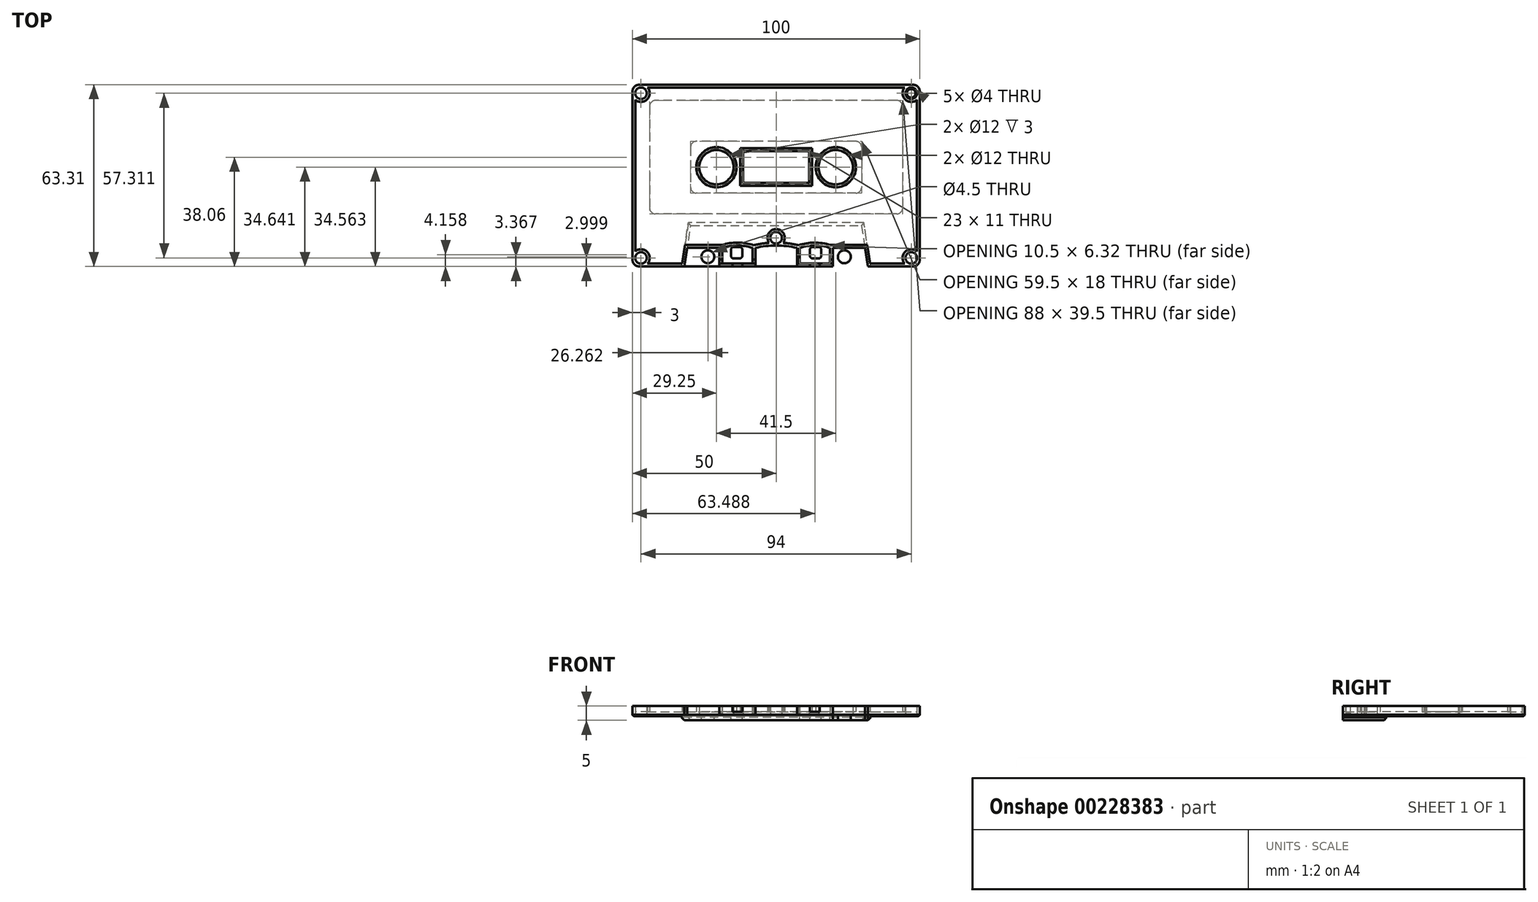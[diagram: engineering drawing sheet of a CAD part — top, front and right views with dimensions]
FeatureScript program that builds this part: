
annotation { "Feature Type Name" : "Feature", "Feature Type Description" : "" }
export const myFeature = defineFeature(function(context is Context, id is Id, definition is map)
    precondition{}
    {
        {
            var Q0;
            Q0=qCreatedBy(makeId("Top.planeOp"),FACE);
            var sketch = newSketch(context, id + "F0", { "sketchPlane" : qUnion([Q0])});
            skLineSegment(sketch, "E0.bottom", {"start": v(-47.5, 0) * mm, "end": v(47.5, 0) * mm});
            skLineSegment(sketch, "E0.top", {"start": v(-47.5, -63.31) * mm, "end": v(47.5, -63.31) * mm});
            skLineSegment(sketch, "E0.left", {"start": v(-50, -2.5) * mm, "end": v(-50, -60.81) * mm});
            skLineSegment(sketch, "E0.right", {"start": v(50, -2.5) * mm, "end": v(50, -60.81) * mm});
            skPoint(sketch, "E0.middle", {"position": v(0, -31.66) * mm});
            skLineSegment(sketch, "E1", {"start": v(0, -65.66) * mm, "end": v(0, 8.32) * mm, "construction": true});
            skLineSegment(sketch, "E2.bottom", {"start": v(42, -5.5) * mm, "end": v(-42, -5.5) * mm});
            skLineSegment(sketch, "E2.top", {"start": v(42, -45) * mm, "end": v(-42, -45) * mm});
            skLineSegment(sketch, "E2.left", {"start": v(44, -7.5) * mm, "end": v(44, -43) * mm});
            skLineSegment(sketch, "E2.right", {"start": v(-44, -7.5) * mm, "end": v(-44, -43) * mm});
            skPoint(sketch, "E2.middle", {"position": v(0, -25.25) * mm});
            skPoint(sketch, "E3.visualSharp", {"position": v(-44, -5.5) * mm});
            skArc(sketch, "E3.filletArc", {"start": v(-42, -5.5) * mm, "mid": v(-43.41, -6.09) * mm, "end": v(-44, -7.5) * mm});
            skPoint(sketch, "E4.visualSharp", {"position": v(-44, -45) * mm});
            skArc(sketch, "E4.filletArc", {"start": v(-44, -43) * mm, "mid": v(-43.41, -44.41) * mm, "end": v(-42, -45) * mm});
            skPoint(sketch, "E5.visualSharp", {"position": v(44, -5.5) * mm});
            skArc(sketch, "E5.filletArc", {"start": v(44, -7.5) * mm, "mid": v(43.41, -6.09) * mm, "end": v(42, -5.5) * mm});
            skPoint(sketch, "E6.visualSharp", {"position": v(44, -45) * mm});
            skArc(sketch, "E6.filletArc", {"start": v(42, -45) * mm, "mid": v(43.41, -44.41) * mm, "end": v(44, -43) * mm});
            skLineSegment(sketch, "E7.bottom", {"start": v(27.75, -19.75) * mm, "end": v(-27.75, -19.75) * mm});
            skLineSegment(sketch, "E7.top", {"start": v(27.75, -37.75) * mm, "end": v(-27.75, -37.75) * mm});
            skLineSegment(sketch, "E7.left", {"start": v(29.75, -21.75) * mm, "end": v(29.75, -35.75) * mm});
            skLineSegment(sketch, "E7.right", {"start": v(-29.75, -21.75) * mm, "end": v(-29.75, -35.75) * mm});
            skPoint(sketch, "E7.middle", {"position": v(0, -28.75) * mm});
            skPoint(sketch, "E8.visualSharp", {"position": v(-29.75, -19.75) * mm});
            skArc(sketch, "E8.filletArc", {"start": v(-27.75, -19.75) * mm, "mid": v(-29.16, -20.33) * mm, "end": v(-29.75, -21.75) * mm});
            skPoint(sketch, "E9.visualSharp", {"position": v(-29.75, -37.75) * mm});
            skArc(sketch, "E9.filletArc", {"start": v(-29.75, -35.75) * mm, "mid": v(-29.16, -37.16) * mm, "end": v(-27.75, -37.75) * mm});
            skPoint(sketch, "E10.visualSharp", {"position": v(29.75, -19.75) * mm});
            skArc(sketch, "E10.filletArc", {"start": v(29.75, -21.75) * mm, "mid": v(29.16, -20.33) * mm, "end": v(27.75, -19.75) * mm});
            skPoint(sketch, "E11.visualSharp", {"position": v(29.75, -37.75) * mm});
            skArc(sketch, "E11.filletArc", {"start": v(27.75, -37.75) * mm, "mid": v(29.16, -37.16) * mm, "end": v(29.75, -35.75) * mm});
            skPoint(sketch, "E12.visualSharp", {"position": v(-50, 0) * mm});
            skArc(sketch, "E12.filletArc", {"start": v(-47.5, 0) * mm, "mid": v(-49.27, -0.73) * mm, "end": v(-50, -2.5) * mm});
            skPoint(sketch, "E13.visualSharp", {"position": v(-50, -63.31) * mm});
            skArc(sketch, "E13.filletArc", {"start": v(-50, -60.81) * mm, "mid": v(-49.27, -62.58) * mm, "end": v(-47.5, -63.31) * mm});
            skPoint(sketch, "E14.visualSharp", {"position": v(50, -63.31) * mm});
            skArc(sketch, "E14.filletArc", {"start": v(47.5, -63.31) * mm, "mid": v(49.27, -62.58) * mm, "end": v(50, -60.81) * mm});
            skPoint(sketch, "E15.visualSharp", {"position": v(50, 0) * mm});
            skArc(sketch, "E15.filletArc", {"start": v(50, -2.5) * mm, "mid": v(49.27, -0.73) * mm, "end": v(47.5, 0) * mm});
            skCircle(sketch, "E16.0", {"center": v(-20.75, -28.75) * mm, "radius": 6 * mm});
            skLineSegment(sketch, "E17.bottom", {"start": v(11.5, -23.17) * mm, "end": v(-11.5, -23.17) * mm});
            skLineSegment(sketch, "E17.top", {"start": v(11.5, -34.17) * mm, "end": v(-11.5, -34.17) * mm});
            skLineSegment(sketch, "E17.left", {"start": v(11.5, -23.17) * mm, "end": v(11.5, -34.17) * mm});
            skLineSegment(sketch, "E17.right", {"start": v(-11.5, -23.17) * mm, "end": v(-11.5, -34.17) * mm});
            skPoint(sketch, "E17.middle", {"position": v(0, -28.67) * mm});
            skLineSegment(sketch, "E18.bottom", {"start": v(-14.74, -56.51) * mm, "end": v(-12.74, -56.51) * mm});
            skLineSegment(sketch, "E18.top", {"start": v(-14.74, -60.51) * mm, "end": v(-12.74, -60.51) * mm});
            skLineSegment(sketch, "E18.left", {"start": v(-15.74, -57.51) * mm, "end": v(-15.74, -59.51) * mm});
            skLineSegment(sketch, "E18.right", {"start": v(-11.74, -57.51) * mm, "end": v(-11.74, -59.51) * mm});
            skPoint(sketch, "E19.visualSharp", {"position": v(-15.74, -56.51) * mm});
            skArc(sketch, "E19.filletArc", {"start": v(-14.74, -56.51) * mm, "mid": v(-15.44, -56.8) * mm, "end": v(-15.74, -57.51) * mm});
            skPoint(sketch, "E20.visualSharp", {"position": v(-11.74, -56.51) * mm});
            skArc(sketch, "E20.filletArc", {"start": v(-11.74, -57.51) * mm, "mid": v(-12.03, -56.8) * mm, "end": v(-12.74, -56.51) * mm});
            skPoint(sketch, "E21.visualSharp", {"position": v(-11.74, -60.51) * mm});
            skArc(sketch, "E21.filletArc", {"start": v(-12.74, -60.51) * mm, "mid": v(-12.03, -60.22) * mm, "end": v(-11.74, -59.51) * mm});
            skPoint(sketch, "E22.visualSharp", {"position": v(-15.74, -60.51) * mm});
            skArc(sketch, "E22.filletArc", {"start": v(-15.74, -59.51) * mm, "mid": v(-15.44, -60.22) * mm, "end": v(-14.74, -60.51) * mm});
            skCircle(sketch, "E23", {"center": v(-23.74, -59.94) * mm, "radius": 2.25 * mm});
            skArc(sketch, "E24.MirrorCS", {"start": v(11.74, -57.51) * mm, "mid": v(12.03, -56.8) * mm, "end": v(12.74, -56.51) * mm});
            skArc(sketch, "E25.MirrorCS", {"start": v(12.74, -60.51) * mm, "mid": v(12.03, -60.22) * mm, "end": v(11.74, -59.51) * mm});
            skArc(sketch, "E26.MirrorCS", {"start": v(14.74, -56.51) * mm, "mid": v(15.44, -56.8) * mm, "end": v(15.74, -57.51) * mm});
            skLineSegment(sketch, "E27.MirrorCS", {"start": v(14.74, -56.51) * mm, "end": v(12.74, -56.51) * mm});
            skArc(sketch, "E28.MirrorCS", {"start": v(15.74, -59.51) * mm, "mid": v(15.44, -60.22) * mm, "end": v(14.74, -60.51) * mm});
            skLineSegment(sketch, "E29.MirrorCS", {"start": v(14.74, -60.51) * mm, "end": v(12.74, -60.51) * mm});
            skLineSegment(sketch, "E30.MirrorCS", {"start": v(15.74, -57.51) * mm, "end": v(15.74, -59.51) * mm});
            skPoint(sketch, "E31.MirrorP", {"position": v(15.74, -56.51) * mm});
            skCircle(sketch, "E32.MirrorC", {"center": v(23.74, -59.94) * mm, "radius": 2.25 * mm});
            skPoint(sketch, "E33.MirrorP", {"position": v(11.74, -56.51) * mm});
            skPoint(sketch, "E34.MirrorP", {"position": v(15.74, -60.51) * mm});
            skLineSegment(sketch, "E35.MirrorCS", {"start": v(11.74, -57.51) * mm, "end": v(11.74, -59.51) * mm});
            skPoint(sketch, "E36.MirrorP", {"position": v(11.74, -60.51) * mm});
            skCircle(sketch, "E37", {"center": v(-47, -60.31) * mm, "radius": 2 * mm});
            skCircle(sketch, "E38.0", {"center": v(-47, -60.31) * mm, "radius": 1.5 * mm});
            skCircle(sketch, "E39", {"center": v(-47, -3) * mm, "radius": 2 * mm});
            skCircle(sketch, "E40.0", {"center": v(-47, -3) * mm, "radius": 1.5 * mm});
            skCircle(sketch, "E41", {"center": v(0, -53.31) * mm, "radius": 2 * mm});
            skCircle(sketch, "E42.0", {"center": v(0, -53.31) * mm, "radius": 1.5 * mm});
            skCircle(sketch, "E43.MirrorC", {"center": v(47, -3) * mm, "radius": 2 * mm});
            skCircle(sketch, "E44.MirrorC", {"center": v(47, -3) * mm, "radius": 1.5 * mm});
            skCircle(sketch, "E45.MirrorC", {"center": v(47, -60.31) * mm, "radius": 1.5 * mm});
            skCircle(sketch, "E46.MirrorC", {"center": v(47, -60.31) * mm, "radius": 2 * mm});
            skLineSegment(sketch, "E47", {"start": v(-32.91, -63.31) * mm, "end": v(-30.5, -48) * mm});
            skLineSegment(sketch, "E48", {"start": v(-30.5, -48) * mm, "end": v(0, -48) * mm});
            skLineSegment(sketch, "E49.MirrorCS", {"start": v(30.5, -48) * mm, "end": v(0, -48) * mm});
            skLineSegment(sketch, "E50.MirrorCS", {"start": v(32.91, -63.31) * mm, "end": v(30.5, -48) * mm});
            skCircle(sketch, "E51.MirrorC", {"center": v(20.75, -28.75) * mm, "radius": 6 * mm});
            skLineSegment(sketch, "E52", {"start": v(-31.9, -63.31) * mm, "end": v(-30.88, -56.81) * mm});
            skLineSegment(sketch, "E53", {"start": v(-30.88, -56.81) * mm, "end": v(-19.74, -56.81) * mm});
            skLineSegment(sketch, "E54", {"start": v(-19.74, -56.81) * mm, "end": v(-19.74, -63.31) * mm});
            skLineSegment(sketch, "E55", {"start": v(-18.74, -62.31) * mm, "end": v(-8.24, -62.31) * mm});
            skLineSegment(sketch, "E56.MirrorCS", {"start": v(19.74, -56.81) * mm, "end": v(19.74, -63.31) * mm});
            skLineSegment(sketch, "E57.MirrorCS", {"start": v(30.88, -56.81) * mm, "end": v(19.74, -56.81) * mm});
            skLineSegment(sketch, "E58.MirrorCS", {"start": v(31.9, -63.31) * mm, "end": v(30.88, -56.81) * mm});
            skLineSegment(sketch, "E59", {"start": v(-8.24, -62.31) * mm, "end": v(-8.24, -56.81) * mm});
            skLineSegment(sketch, "E60", {"start": v(-18.74, -56.81) * mm, "end": v(-18.74, -62.31) * mm});
            skPoint(sketch, "E61.orphan", {"position": v(-19.74, -62.31) * mm});
            skLineSegment(sketch, "E62", {"start": v(-7.24, -63.31) * mm, "end": v(-7.24, -56.81) * mm});
            skLineSegment(sketch, "E63.MirrorCS", {"start": v(7.24, -63.31) * mm, "end": v(7.24, -56.81) * mm});
            skLineSegment(sketch, "E64.MirrorCS", {"start": v(8.24, -62.31) * mm, "end": v(8.24, -56.81) * mm});
            skLineSegment(sketch, "E65.MirrorCS", {"start": v(18.74, -62.31) * mm, "end": v(8.24, -62.31) * mm});
            skLineSegment(sketch, "E66.MirrorCS", {"start": v(18.74, -56.81) * mm, "end": v(18.74, -62.31) * mm});
            skArc(sketch, "E67", {"start": v(7.24, -56.81) * mm, "mid": v(0, -55.99) * mm, "end": v(-7.24, -56.81) * mm});
            skArc(sketch, "E68", {"start": v(-8.24, -56.81) * mm, "mid": v(-13.49, -56) * mm, "end": v(-18.74, -56.81) * mm});
            skArc(sketch, "E69.MirrorCS", {"start": v(8.24, -56.81) * mm, "mid": v(13.49, -56) * mm, "end": v(18.74, -56.81) * mm});
            skSolve(sketch);
        }
        {
            var Q0;
            Q0=makeQuery(id+"F0.imprint","IMPRINT",FACE,{"disambiguationData":[TD([[makeQuery(id+"F0.imprint","IMPRINT",EDGE,{"derivedFrom":sQuery(id+"F0.wireOp",EDGE,"E0.bottom")}),-1.0]])]});
            var Q1;
            Q1=makeQuery(id+"F0.imprint","IMPRINT",FACE,{"disambiguationData":[TD([[makeQuery(id+"F0.imprint","IMPRINT",EDGE,{"derivedFrom":sQuery(id+"F0.wireOp",EDGE,"E44.MirrorC")}),-1.0]])]});
            var Q2;
            Q2=makeQuery(id+"F0.imprint","IMPRINT",FACE,{"disambiguationData":[TD([[makeQuery(id+"F0.imprint","IMPRINT",EDGE,{"derivedFrom":sQuery(id+"F0.wireOp",EDGE,"E43.MirrorC")}),-1.0]])]});
            var Q3;
            Q3=makeQuery(id+"F0.imprint","IMPRINT",FACE,{"disambiguationData":[TD([[makeQuery(id+"F0.imprint","IMPRINT",EDGE,{"derivedFrom":sQuery(id+"F0.wireOp",EDGE,"E45.MirrorC")}),-1.0]])]});
            var Q4;
            Q4=makeQuery(id+"F0.imprint","IMPRINT",FACE,{"disambiguationData":[TD([[makeQuery(id+"F0.imprint","IMPRINT",EDGE,{"derivedFrom":sQuery(id+"F0.wireOp",EDGE,"E45.MirrorC")}),1.0]])]});
            var Q5;
            Q5=makeQuery(id+"F0.imprint","IMPRINT",FACE,{"disambiguationData":[TD([[makeQuery(id+"F0.imprint","IMPRINT",EDGE,{"derivedFrom":sQuery(id+"F0.wireOp",EDGE,"E41")}),-1.0]])]});
            var Q6;
            Q6=makeQuery(id+"F0.imprint","IMPRINT",FACE,{"disambiguationData":[TD([[makeQuery(id+"F0.imprint","IMPRINT",EDGE,{"derivedFrom":sQuery(id+"F0.wireOp",EDGE,"E23")}),-1.0]])]});
            var Q7;
            Q7=makeQuery(id+"F0.imprint","IMPRINT",FACE,{"disambiguationData":[TD([[makeQuery(id+"F0.imprint","IMPRINT",EDGE,{"derivedFrom":sQuery(id+"F0.wireOp",EDGE,"E32.MirrorC")}),1.0]])]});
            var Q8;
            Q8=makeQuery(id+"F0.imprint","IMPRINT",FACE,{"disambiguationData":[TD([[makeQuery(id+"F0.imprint","IMPRINT",EDGE,{"derivedFrom":sQuery(id+"F0.wireOp",EDGE,"E42.0")}),1.0]])]});
            var Q9;
            Q9=makeQuery(id+"F0.imprint","IMPRINT",FACE,{"disambiguationData":[TD([[makeQuery(id+"F0.imprint","IMPRINT",EDGE,{"derivedFrom":sQuery(id+"F0.wireOp",EDGE,"E18.bottom")}),1.0]])]});
            var Q10;
            Q10=makeQuery(id+"F0.imprint","IMPRINT",FACE,{"disambiguationData":[TD([[makeQuery(id+"F0.imprint","IMPRINT",EDGE,{"derivedFrom":sQuery(id+"F0.wireOp",EDGE,"E37")}),1.0]])]});
            var Q11;
            Q11=makeQuery(id+"F0.imprint","IMPRINT",FACE,{"disambiguationData":[TD([[makeQuery(id+"F0.imprint","IMPRINT",EDGE,{"derivedFrom":sQuery(id+"F0.wireOp",EDGE,"E41")}),1.0]])]});
            var Q12;
            Q12=makeQuery(id+"F0.imprint","IMPRINT",FACE,{"disambiguationData":[TD([[makeQuery(id+"F0.imprint","IMPRINT",EDGE,{"derivedFrom":sQuery(id+"F0.wireOp",EDGE,"E24.MirrorCS")}),1.0]])]});
            var Q13;
            Q13=makeQuery(id+"F0.imprint","IMPRINT",FACE,{"disambiguationData":[TD([[makeQuery(id+"F0.imprint","IMPRINT",EDGE,{"derivedFrom":sQuery(id+"F0.wireOp",EDGE,"E38.0")}),1.0]])]});
            var Q14;
            {var subQ0=sQuery(id+"F0.wireOp",EDGE,"E62");Q14=makeQuery(id+"F0.imprint","IMPRINT",FACE,{"disambiguationData":[TD([[makeQuery(id+"F0.imprint","IMPRINT",EDGE,{"derivedFrom":subQ0}),-1.0]])]});}
            var Q15;
            Q15=makeQuery(id+"F0.imprint","IMPRINT",FACE,{"disambiguationData":[TD([[makeQuery(id+"F0.imprint","IMPRINT",EDGE,{"derivedFrom":sQuery(id+"F0.wireOp",EDGE,"E40.0")}),1.0]])]});
            var Q16;
            Q16=makeQuery(id+"F0.imprint","IMPRINT",FACE,{"disambiguationData":[TD([[makeQuery(id+"F0.imprint","IMPRINT",EDGE,{"derivedFrom":sQuery(id+"F0.wireOp",EDGE,"E39")}),1.0]])]});
            var Q17;
            Q17=makeQuery(id+"F0.imprint","IMPRINT",FACE,{"disambiguationData":[TD([[makeQuery(id+"F0.imprint","IMPRINT",EDGE,{"derivedFrom":sQuery(id+"F0.wireOp",EDGE,"E7.bottom")}),1.0]])]});
            extrude(context, id + "F1", {"entities" : qUnion([Q0, Q1, Q2, Q3, Q4, Q5, Q6, Q7, Q8, Q9, Q10, Q11, Q12, Q13, Q14, Q15, Q16, Q17]), "oppositeDirection" : true, "depth" : .6 * mm});
        }
        {
            var Q0;
            Q0=makeQuery(id+"F0.imprint","IMPRINT",FACE,{"disambiguationData":[TD([[makeQuery(id+"F0.imprint","IMPRINT",EDGE,{"derivedFrom":sQuery(id+"F0.wireOp",EDGE,"E2.bottom")}),1.0]])]});
            extrude(context, id + "F2", {"entities" : qUnion([Q0]), "oppositeDirection" : true, "depth" : .3 * mm});
        }
        {
            var Q0;
            Q0=makeQuery(id+"F0.imprint","IMPRINT",FACE,{"disambiguationData":[TD([[makeQuery(id+"F0.imprint","IMPRINT",EDGE,{"derivedFrom":sQuery(id+"F0.wireOp",EDGE,"E41")}),-1.0]])]});
            var Q1;
            Q1=makeQuery(id+"F0.imprint","IMPRINT",FACE,{"disambiguationData":[TD([[makeQuery(id+"F0.imprint","IMPRINT",EDGE,{"derivedFrom":sQuery(id+"F0.wireOp",EDGE,"E23")}),-1.0]])]});
            var Q2;
            {var subQ0=sQuery(id+"F0.wireOp",EDGE,"E62");Q2=makeQuery(id+"F0.imprint","IMPRINT",FACE,{"disambiguationData":[TD([[makeQuery(id+"F0.imprint","IMPRINT",EDGE,{"derivedFrom":subQ0}),-1.0]])]});}
            var Q3;
            Q3=makeQuery(id+"F0.imprint","IMPRINT",FACE,{"disambiguationData":[TD([[makeQuery(id+"F0.imprint","IMPRINT",EDGE,{"derivedFrom":sQuery(id+"F0.wireOp",EDGE,"E18.bottom")}),1.0]])]});
            var Q4;
            Q4=makeQuery(id+"F0.imprint","IMPRINT",FACE,{"disambiguationData":[TD([[makeQuery(id+"F0.imprint","IMPRINT",EDGE,{"derivedFrom":sQuery(id+"F0.wireOp",EDGE,"E42.0")}),1.0]])]});
            var Q5;
            Q5=makeQuery(id+"F0.imprint","IMPRINT",FACE,{"disambiguationData":[TD([[makeQuery(id+"F0.imprint","IMPRINT",EDGE,{"derivedFrom":sQuery(id+"F0.wireOp",EDGE,"E41")}),1.0]])]});
            var Q6;
            Q6=makeQuery(id+"F0.imprint","IMPRINT",FACE,{"disambiguationData":[TD([[makeQuery(id+"F0.imprint","IMPRINT",EDGE,{"derivedFrom":sQuery(id+"F0.wireOp",EDGE,"E24.MirrorCS")}),1.0]])]});
            var Q7;
            Q7=makeQuery(id+"F0.imprint","IMPRINT",FACE,{"disambiguationData":[TD([[makeQuery(id+"F0.imprint","IMPRINT",EDGE,{"derivedFrom":sQuery(id+"F0.wireOp",EDGE,"E32.MirrorC")}),1.0]])]});
            extrude(context, id + "F3", {"entities" : qUnion([Q0, Q1, Q2, Q3, Q4, Q5, Q6, Q7]), "operationType" : NewBodyOperationType.ADD, "oppositeDirection" : true, "depth" : 2 * mm});
        }
        {
            var Q0;
            Q0=makeQuery(id+"F0.imprint","IMPRINT",FACE,{"disambiguationData":[TD([[makeQuery(id+"F0.imprint","IMPRINT",EDGE,{"derivedFrom":sQuery(id+"F0.wireOp",EDGE,"E2.bottom")}),1.0]])]});
            var Q1;
            Q1=makeQuery(id+"F0.imprint","IMPRINT",FACE,{"disambiguationData":[TD([[makeQuery(id+"F0.imprint","IMPRINT",EDGE,{"derivedFrom":sQuery(id+"F0.wireOp",EDGE,"E0.bottom")}),-1.0]])]});
            var Q2;
            Q2=makeQuery(id+"F0.imprint","IMPRINT",FACE,{"disambiguationData":[TD([[makeQuery(id+"F0.imprint","IMPRINT",EDGE,{"derivedFrom":sQuery(id+"F0.wireOp",EDGE,"E41")}),-1.0]])]});
            var Q3;
            Q3=makeQuery(id+"F0.imprint","IMPRINT",FACE,{"disambiguationData":[TD([[makeQuery(id+"F0.imprint","IMPRINT",EDGE,{"derivedFrom":sQuery(id+"F0.wireOp",EDGE,"E7.bottom")}),1.0]])]});
            extrude(context, id + "F4", {"entities" : qUnion([Q0, Q1, Q2, Q3]), "depth" : 3 * mm});
        }
        {
            var Q0;
            Q0=makeQuery(id+"F4.opExtrude","CAP_FACE",FACE,{"disambiguationData":[OSD([sQuery(id+"F0.wireOp",EDGE,"E0.bottom"),sQuery(id+"F0.wireOp",EDGE,"E0.top"),sQuery(id+"F0.wireOp",EDGE,"E0.left"),sQuery(id+"F0.wireOp",EDGE,"E0.right"),sQuery(id+"F0.wireOp",EDGE,"E12.filletArc"),sQuery(id+"F0.wireOp",EDGE,"E13.filletArc"),sQuery(id+"F0.wireOp",EDGE,"E14.filletArc"),sQuery(id+"F0.wireOp",EDGE,"E15.filletArc"),sQuery(id+"F0.wireOp",EDGE,"E16.0"),sQuery(id+"F0.wireOp",EDGE,"E17.bottom"),sQuery(id+"F0.wireOp",EDGE,"E17.top"),sQuery(id+"F0.wireOp",EDGE,"E17.left"),sQuery(id+"F0.wireOp",EDGE,"E17.right"),sQuery(id+"F0.wireOp",EDGE,"E37"),sQuery(id+"F0.wireOp",EDGE,"E39"),sQuery(id+"F0.wireOp",EDGE,"E41"),sQuery(id+"F0.wireOp",EDGE,"E43.MirrorC"),sQuery(id+"F0.wireOp",EDGE,"E46.MirrorC"),sQuery(id+"F0.wireOp",EDGE,"E51.MirrorC"),sQuery(id+"F0.wireOp",EDGE,"E52"),sQuery(id+"F0.wireOp",EDGE,"E53"),sQuery(id+"F0.wireOp",EDGE,"E54"),sQuery(id+"F0.wireOp",EDGE,"E55"),sQuery(id+"F0.wireOp",EDGE,"E56.MirrorCS"),sQuery(id+"F0.wireOp",EDGE,"E57.MirrorCS"),sQuery(id+"F0.wireOp",EDGE,"E58.MirrorCS"),sQuery(id+"F0.wireOp",EDGE,"E59"),sQuery(id+"F0.wireOp",EDGE,"E60"),sQuery(id+"F0.wireOp",EDGE,"E62"),sQuery(id+"F0.wireOp",EDGE,"E63.MirrorCS"),sQuery(id+"F0.wireOp",EDGE,"E64.MirrorCS"),sQuery(id+"F0.wireOp",EDGE,"E65.MirrorCS"),sQuery(id+"F0.wireOp",EDGE,"E66.MirrorCS"),sQuery(id+"F0.wireOp",EDGE,"E67"),sQuery(id+"F0.wireOp",EDGE,"E68"),sQuery(id+"F0.wireOp",EDGE,"E69.MirrorCS")])],"isStart":false});
            shell(context, id + "F5", {"entities" : qUnion([Q0]), "thickness" : 1 * mm});
        }
        {
            var Q0;
            {var subQ0=sQuery(id+"F0.wireOp",EDGE,"E0.top");Q0=makeQuery(id+"F4.opExtrude","SWEPT_FACE",FACE,{"disambiguationData":[OSD([subQ0]),TDD([makeQuery(id+"F0.imprint","IMPRINT",EDGE,{"disambiguationData":[TD([[makeQuery(id+"F0.imprint","INTERSECT",VERTEX,{"derivedFrom":[subQ0,sQuery(id+"F0.wireOp",EDGE,"E54")]}),-1.0]])],"derivedFrom":subQ0})])]});}
            var sketch = newSketch(context, id + "F6", { "sketchPlane" : qUnion([Q0])});
            skLineSegment(sketch, "E70", {"start": v(0, 0) * mm, "end": v(0, 6.2) * mm, "construction": true});
            skLineSegment(sketch, "E71.bottom", {"start": v(-11.74, 1) * mm, "end": v(-15.24, 1) * mm});
            skLineSegment(sketch, "E71.top", {"start": v(-11.74, 5) * mm, "end": v(-15.24, 5) * mm});
            skLineSegment(sketch, "E71.left", {"start": v(-11.74, 1) * mm, "end": v(-11.74, 5) * mm});
            skLineSegment(sketch, "E71.right", {"start": v(-15.24, 1) * mm, "end": v(-15.24, 5) * mm});
            skPoint(sketch, "E71.middle", {"position": v(-13.49, 3) * mm});
            skLineSegment(sketch, "E72.MirrorCS", {"start": v(11.74, 1) * mm, "end": v(11.74, 5) * mm});
            skLineSegment(sketch, "E73.MirrorCS", {"start": v(11.74, 5) * mm, "end": v(15.24, 5) * mm});
            skLineSegment(sketch, "E74.MirrorCS", {"start": v(15.24, 1) * mm, "end": v(15.24, 5) * mm});
            skLineSegment(sketch, "E75.MirrorCS", {"start": v(11.74, 1) * mm, "end": v(15.24, 1) * mm});
            skSolve(sketch);
        }
        {
            var Q0;
            {var subQ0=sQuery(id+"F6.wireOp",EDGE,"E71.bottom");Q0=makeQuery(id+"F6.imprint","IMPRINT",FACE,{"disambiguationData":[TD([[makeQuery(id+"F6.imprint","IMPRINT",EDGE,{"derivedFrom":subQ0}),-1.0]])]});}
            var Q1;
            Q1=makeQuery(id+"F6.imprint","IMPRINT",FACE,{"disambiguationData":[TD([[makeQuery(id+"F6.imprint","IMPRINT",EDGE,{"derivedFrom":sQuery(id+"F6.wireOp",EDGE,"E72.MirrorCS")}),-1.0]])]});
            var Q2;
            {var subQ0=sQuery(id+"F6.wireOp",EDGE,"E71.top");Q2=makeQuery(id+"F6.imprint","IMPRINT",FACE,{"disambiguationData":[TD([[makeQuery(id+"F6.imprint","IMPRINT",EDGE,{"derivedFrom":subQ0}),1.0]])]});}
            extrude(context, id + "F7", {"entities" : qUnion([Q0, Q1, Q2]), "operationType" : NewBodyOperationType.REMOVE, "oppositeDirection" : true, "depth" : 3.6 * mm});
        }
        {
            var Q0;
            Q0=qCreatedBy(makeId("Right.planeOp"),FACE);
            var sketch = newSketch(context, id + "F8", { "sketchPlane" : qUnion([Q0])});
            skLineSegment(sketch, "E76.0", {"start": v(-62.31, 3) * mm, "end": v(-62.31, 0) * mm});
            skLineSegment(sketch, "E77.0", {"start": v(-56.81, 3) * mm, "end": v(-62.31, 3) * mm});
            skLineSegment(sketch, "E78.0", {"start": v(-56.81, 0) * mm, "end": v(-62.31, 0) * mm});
            skLineSegment(sketch, "E79", {"start": v(-60.81, 3) * mm, "end": v(-60.81, 0.5) * mm});
            skLineSegment(sketch, "E80", {"start": v(-60.81, 0.5) * mm, "end": v(-62.31, 0.5) * mm});
            skSolve(sketch);
        }
        {
            var Q0;
            {var subQ4=sQuery(id+"F8.wireOp",EDGE,"E79");Q0=makeQuery(id+"F8.imprint","IMPRINT",FACE,{"disambiguationData":[TD([[makeQuery(id+"F8.imprint","IMPRINT",EDGE,{"derivedFrom":subQ4}),-1.0]])]});}
            extrude(context, id + "F9", {"entities" : qUnion([Q0]), "operationType" : NewBodyOperationType.REMOVE, "endBound" : BoundingType.SYMMETRIC, "oppositeDirection" : true, "depth" : 43.8 * mm});
        }
        {
            var Q0;
            Q0=makeQuery(id+"F1.opExtrude","CAP_EDGE",EDGE,{"disambiguationData":[OSD([sQuery(id+"F0.wireOp",EDGE,"E0.bottom")])],"isStart":false});
            fillet(context, id + "F10", {"entities" : qUnion([Q0]), "radius" : 1 * mm, "tangentPropagation" : true, "allowEdgeOverflow" : false});
        }
        {
            var Q0;
            Q0=makeQuery(id+"F1.opExtrude","CAP_EDGE",EDGE,{"disambiguationData":[OSD([sQuery(id+"F0.wireOp",EDGE,"E51.MirrorC")])],"isStart":false});
            var Q1;
            Q1=makeQuery(id+"F1.opExtrude","CAP_EDGE",EDGE,{"disambiguationData":[OSD([sQuery(id+"F0.wireOp",EDGE,"E17.bottom")])],"isStart":false});
            var Q2;
            Q2=makeQuery(id+"F1.opExtrude","CAP_EDGE",EDGE,{"disambiguationData":[OSD([sQuery(id+"F0.wireOp",EDGE,"E17.left")])],"isStart":false});
            var Q3;
            Q3=makeQuery(id+"F1.opExtrude","CAP_EDGE",EDGE,{"disambiguationData":[OSD([sQuery(id+"F0.wireOp",EDGE,"E17.top")])],"isStart":false});
            var Q4;
            Q4=makeQuery(id+"F1.opExtrude","CAP_EDGE",EDGE,{"disambiguationData":[OSD([sQuery(id+"F0.wireOp",EDGE,"E17.right")])],"isStart":false});
            var Q5;
            Q5=makeQuery(id+"F1.opExtrude","CAP_EDGE",EDGE,{"disambiguationData":[OSD([sQuery(id+"F0.wireOp",EDGE,"E16.0")])],"isStart":false});
            chamfer(context, id + "F11", {"entities" : qUnion([Q0, Q1, Q2, Q3, Q4, Q5]), "width" : .4 * mm, "tangentPropagation" : true});
        }
        {
            var Q0;
            Q0=makeQuery(id+"F3.opExtrude","CAP_EDGE",EDGE,{"disambiguationData":[OSD([sQuery(id+"F0.wireOp",EDGE,"E48"),sQuery(id+"F0.wireOp",EDGE,"E49.MirrorCS")])],"isStart":false});
            var Q1;
            Q1=makeQuery(id+"F3.opExtrude","CAP_EDGE",EDGE,{"disambiguationData":[OSD([sQuery(id+"F0.wireOp",EDGE,"E50.MirrorCS")])],"isStart":false});
            var Q2;
            Q2=makeQuery(id+"F3.opExtrude","CAP_EDGE",EDGE,{"disambiguationData":[OSD([sQuery(id+"F0.wireOp",EDGE,"E47")])],"isStart":false});
            chamfer(context, id + "F12", {"entities" : qUnion([Q0, Q1, Q2]), "width" : 1 * mm, "tangentPropagation" : true});
        }
    });
